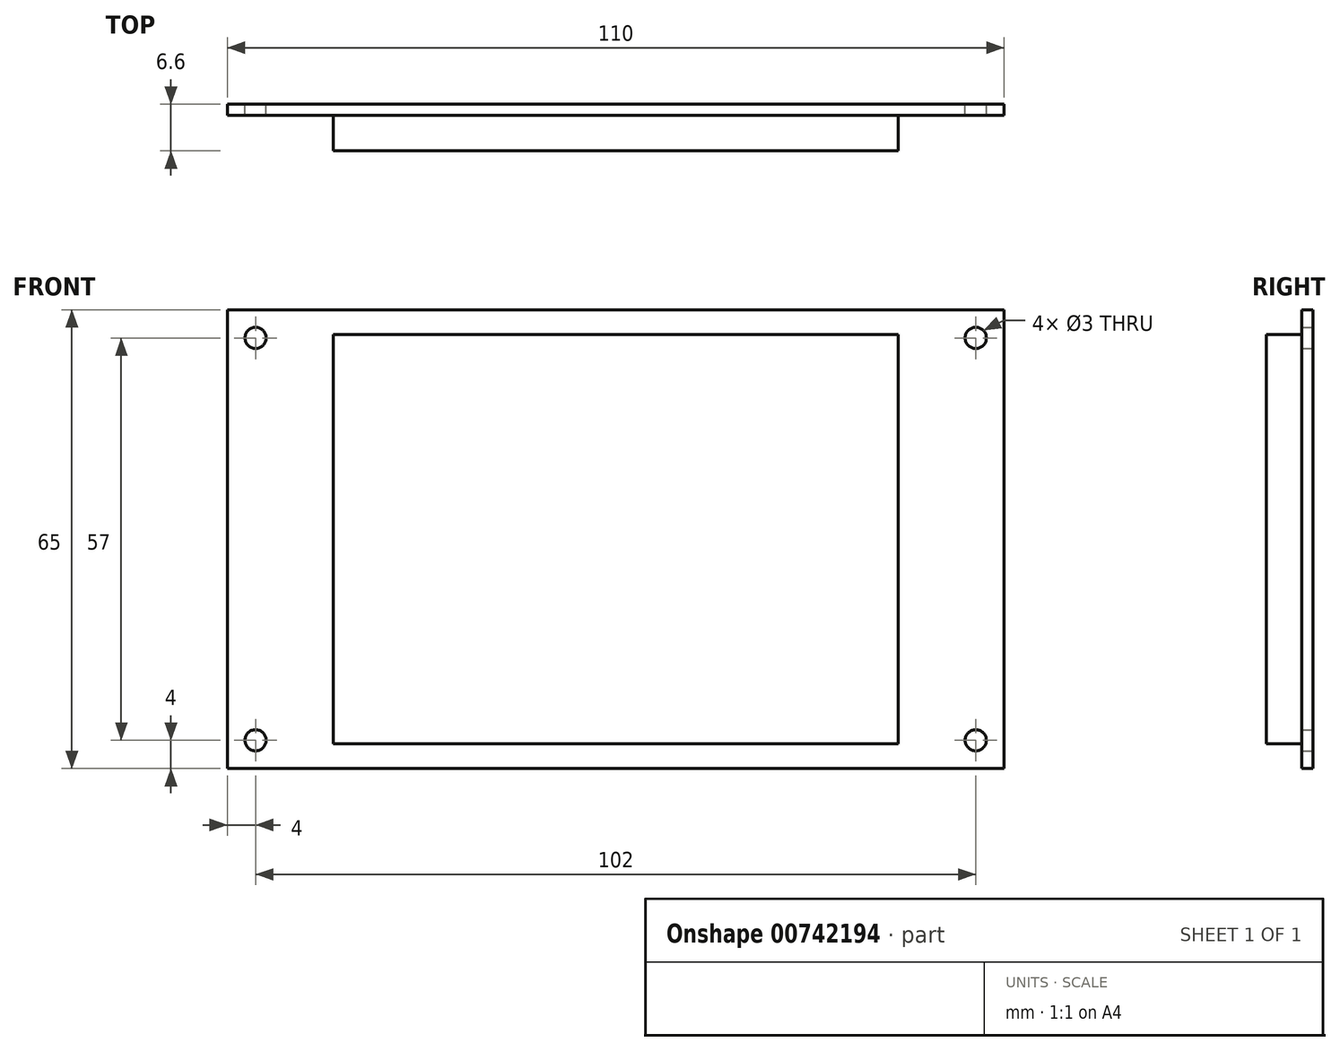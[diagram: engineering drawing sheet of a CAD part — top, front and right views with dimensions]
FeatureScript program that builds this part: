
annotation { "Feature Type Name" : "Feature", "Feature Type Description" : "" }
export const myFeature = defineFeature(function(context is Context, id is Id, definition is map)
    precondition{}
    {
        {
            var Q0;
            Q0=qCreatedBy(makeId("Front.planeOp"),FACE);
            var sketch = newSketch(context, id + "F0", { "sketchPlane" : qUnion([Q0])});
            skLineSegment(sketch, "E0.bottom", {"start": v(0, 0) * mm, "end": v(110, 0) * mm});
            skLineSegment(sketch, "E0.top", {"start": v(0, 65) * mm, "end": v(110, 65) * mm});
            skLineSegment(sketch, "E0.left", {"start": v(0, 0) * mm, "end": v(0, 65) * mm});
            skLineSegment(sketch, "E0.right", {"start": v(110, 0) * mm, "end": v(110, 65) * mm});
            skCircle(sketch, "E1", {"center": v(4, 61) * mm, "radius": 1.5 * mm});
            skLineSegment(sketch, "E2", {"start": v(55, 65) * mm, "end": v(55, 0) * mm, "construction": true});
            skLineSegment(sketch, "E3", {"start": v(0, 32.5) * mm, "end": v(110, 32.5) * mm, "construction": true});
            skCircle(sketch, "E4.MirrorC", {"center": v(106, 61) * mm, "radius": 1.5 * mm});
            skCircle(sketch, "E5.MirrorC", {"center": v(106, 4) * mm, "radius": 1.5 * mm});
            skCircle(sketch, "E6.MirrorC", {"center": v(4, 4) * mm, "radius": 1.5 * mm});
            skSolve(sketch);
        }
        {
            var Q0;
            Q0 = qSketchRegion(id + "F0", true);
            extrude(context, id + "F1", {"entities" : qUnion([Q0]), "depth" : 1.6 * mm, "offsetDistance" : 25 * mm});
        }
        {
            var Q0;
            Q0=makeQuery(id+"F1.opExtrude","CAP_FACE",FACE,{"disambiguationData":[OSD([sQuery(id+"F0.wireOp",EDGE,"E0.bottom"),sQuery(id+"F0.wireOp",EDGE,"E0.top"),sQuery(id+"F0.wireOp",EDGE,"E0.left"),sQuery(id+"F0.wireOp",EDGE,"E0.right"),sQuery(id+"F0.wireOp",EDGE,"E1"),sQuery(id+"F0.wireOp",EDGE,"E4.MirrorC"),sQuery(id+"F0.wireOp",EDGE,"E5.MirrorC"),sQuery(id+"F0.wireOp",EDGE,"E6.MirrorC")])],"isStart":false});
            var sketch = newSketch(context, id + "F2", { "sketchPlane" : qUnion([Q0])});
            skLineSegment(sketch, "E7.bottom", {"start": v(15, 3.5) * mm, "end": v(95, 3.5) * mm});
            skLineSegment(sketch, "E7.top", {"start": v(15, 61.5) * mm, "end": v(95, 61.5) * mm});
            skLineSegment(sketch, "E7.left", {"start": v(15, 3.5) * mm, "end": v(15, 61.5) * mm});
            skLineSegment(sketch, "E7.right", {"start": v(95, 3.5) * mm, "end": v(95, 61.5) * mm});
            skSolve(sketch);
        }
        {
            var Q0;
            Q0 = qSketchRegion(id + "F2", true);
            extrude(context, id + "F3", {"entities" : qUnion([Q0]), "operationType" : NewBodyOperationType.ADD, "depth" : 5 * mm, "offsetDistance" : 25 * mm});
        }
    });
